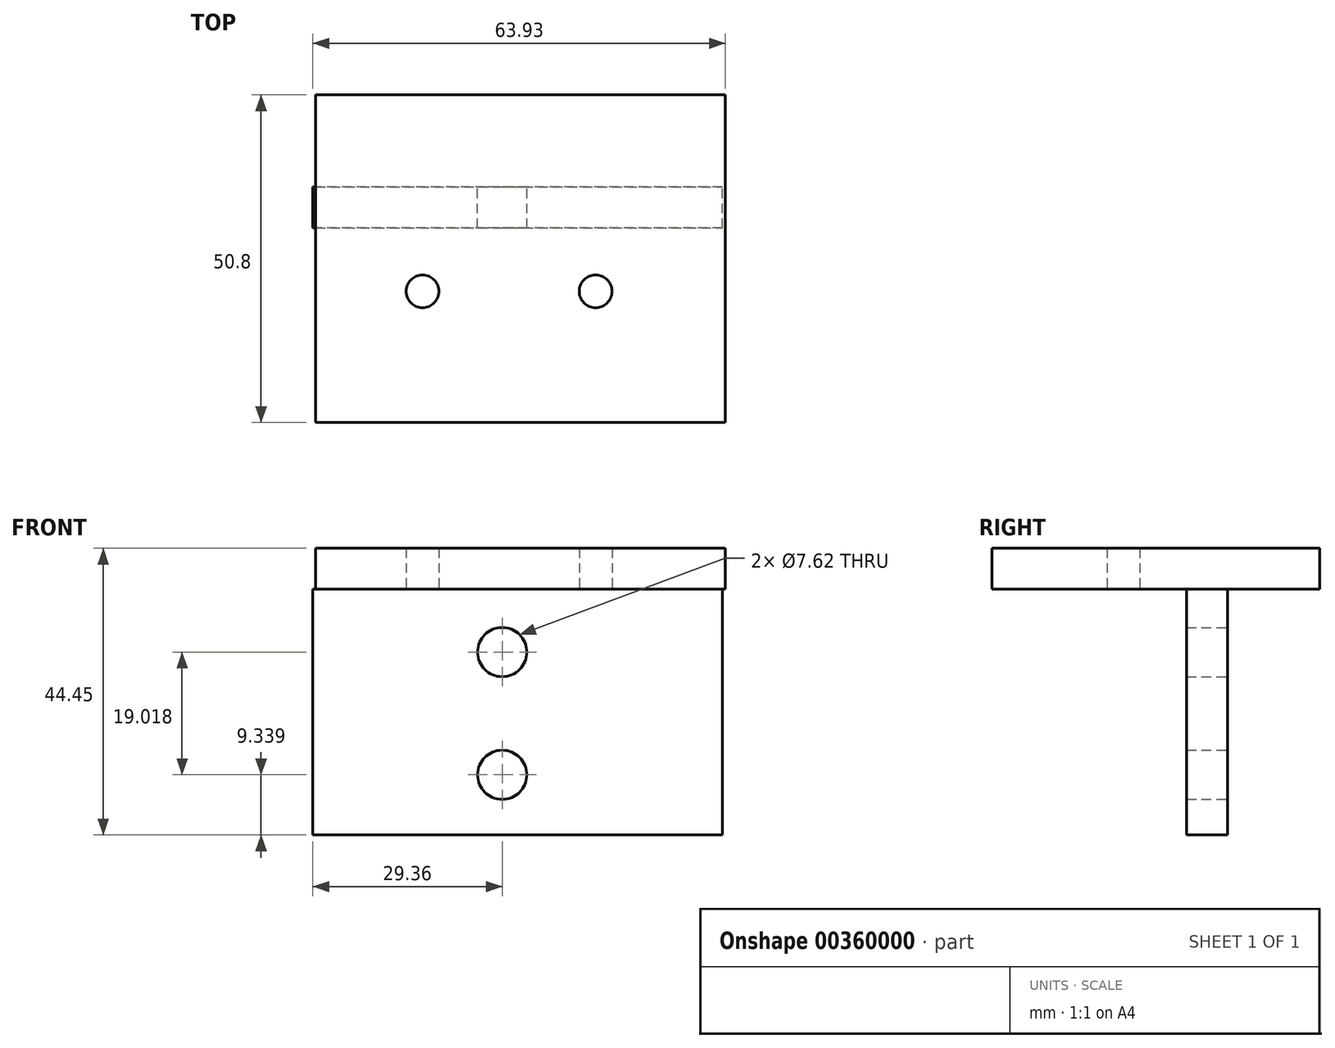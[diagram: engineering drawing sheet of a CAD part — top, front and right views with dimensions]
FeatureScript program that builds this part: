
annotation { "Feature Type Name" : "Feature", "Feature Type Description" : "" }
export const myFeature = defineFeature(function(context is Context, id is Id, definition is map)
    precondition{}
    {
        {
            var Q0;
            Q0=qCreatedBy(makeId("Top.planeOp"),FACE);
            var sketch = newSketch(context, id + "F0", { "sketchPlane" : qUnion([Q0])});
            skLineSegment(sketch, "E0", {"start": v(-28.93, 14.29) * mm, "end": v(34.57, 14.29) * mm});
            skLineSegment(sketch, "E1", {"start": v(34.57, 14.29) * mm, "end": v(34.57, -36.51) * mm});
            skLineSegment(sketch, "E2", {"start": v(34.57, -36.51) * mm, "end": v(-28.93, -36.51) * mm});
            skLineSegment(sketch, "E3", {"start": v(-28.93, -36.51) * mm, "end": v(-28.93, 14.29) * mm});
            skCircle(sketch, "E4", {"center": v(-12.35, -16.17) * mm, "radius": 2.54 * mm});
            skCircle(sketch, "E5", {"center": v(14.48, -16.17) * mm, "radius": 2.54 * mm});
            skSolve(sketch);
        }
        {
            var Q0;
            Q0=qCreatedBy(makeId("Front.planeOp"),FACE);
            var sketch = newSketch(context, id + "F1", { "sketchPlane" : qUnion([Q0])});
            skLineSegment(sketch, "E6", {"start": v(-29.36, 0) * mm, "end": v(34.14, 0) * mm});
            skLineSegment(sketch, "E7", {"start": v(34.14, 0) * mm, "end": v(34.14, -38.1) * mm});
            skLineSegment(sketch, "E8", {"start": v(34.14, -38.1) * mm, "end": v(-29.36, -38.1) * mm});
            skLineSegment(sketch, "E9", {"start": v(-29.36, -38.1) * mm, "end": v(-29.36, 0) * mm});
            skCircle(sketch, "E10", {"center": v(0, -9.74) * mm, "radius": 3.81 * mm});
            skCircle(sketch, "E11", {"center": v(0, -28.76) * mm, "radius": 3.81 * mm});
            skSolve(sketch);
        }
        {
            var Q0;
            Q0=makeQuery(id+"F0.imprint","IMPRINT",FACE,{"disambiguationData":[TD([[makeQuery(id+"F0.imprint","IMPRINT",EDGE,{"derivedFrom":sQuery(id+"F0.wireOp",EDGE,"E0")}),-1.0]])]});
            extrude(context, id + "F2", {"entities" : qUnion([Q0]), "depth" : 6.35 * mm});
        }
        {
            var Q0;
            Q0=makeQuery(id+"F1.imprint","IMPRINT",FACE,{"disambiguationData":[TD([[makeQuery(id+"F1.imprint","IMPRINT",EDGE,{"derivedFrom":sQuery(id+"F1.wireOp",EDGE,"E6")}),-1.0]])]});
            extrude(context, id + "F3", {"entities" : qUnion([Q0]), "operationType" : NewBodyOperationType.ADD, "depth" : 6.35 * mm});
        }
    });
